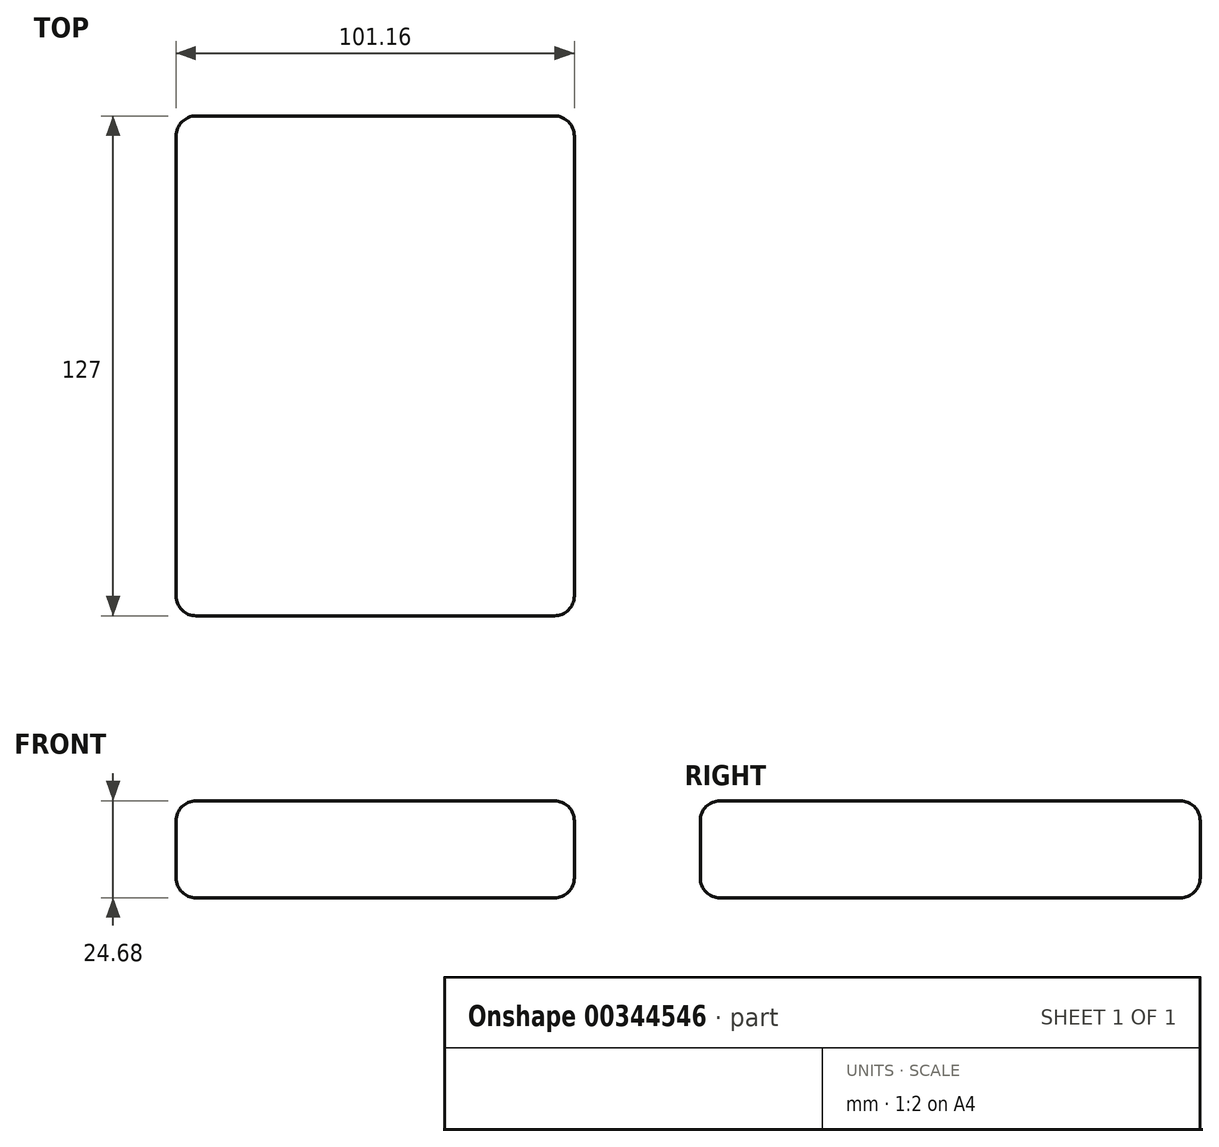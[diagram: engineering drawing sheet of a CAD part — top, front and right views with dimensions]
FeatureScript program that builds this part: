
annotation { "Feature Type Name" : "Feature", "Feature Type Description" : "" }
export const myFeature = defineFeature(function(context is Context, id is Id, definition is map)
    precondition{}
    {
        {
            var Q0;
            Q0=qCreatedBy(makeId("Front.planeOp"),FACE);
            var sketch = newSketch(context, id + "F0", { "sketchPlane" : qUnion([Q0])});
            skLineSegment(sketch, "E0.bottom", {"start": v(-50.58, 12.34) * mm, "end": v(50.58, 12.34) * mm});
            skLineSegment(sketch, "E0.top", {"start": v(-50.58, -12.34) * mm, "end": v(50.58, -12.34) * mm});
            skLineSegment(sketch, "E0.left", {"start": v(-50.58, 12.34) * mm, "end": v(-50.58, -12.34) * mm});
            skLineSegment(sketch, "E0.right", {"start": v(50.58, 12.34) * mm, "end": v(50.58, -12.34) * mm});
            skPoint(sketch, "E0.middle", {"position": v(0, 0) * mm});
            skSolve(sketch);
        }
        {
            var Q0;
            Q0 = qSketchRegion(id + "F0", true);
            var Q1;
            Q1 = qSketchRegion(id + "FBLzmxZTQiUzEOE_0", true);
            extrude(context, id + "F1", {"entities" : qUnion([Q0, Q1]), "endBound" : BoundingType.SYMMETRIC, "depth" : 127 * mm});
        }
        {
            var Q0;
            Q0=makeQuery(id+"F1.opExtrude","CAP_FACE",FACE,{"disambiguationData":[OSD([sQuery(id+"F0.wireOp",EDGE,"E0.bottom"),sQuery(id+"F0.wireOp",EDGE,"E0.top"),sQuery(id+"F0.wireOp",EDGE,"E0.left"),sQuery(id+"F0.wireOp",EDGE,"E0.right")])],"isStart":false});
            var Q1;
            Q1=makeQuery(id+"F1.opExtrude","SWEPT_FACE",FACE,{"disambiguationData":[OSD([sQuery(id+"F0.wireOp",EDGE,"E0.right")])]});
            var Q2;
            Q2=makeQuery(id+"F1.opExtrude","SWEPT_FACE",FACE,{"disambiguationData":[OSD([sQuery(id+"F0.wireOp",EDGE,"E0.left")])]});
            var Q3;
            Q3=makeQuery(id+"F1.opExtrude","CAP_FACE",FACE,{"disambiguationData":[OSD([sQuery(id+"F0.wireOp",EDGE,"E0.bottom"),sQuery(id+"F0.wireOp",EDGE,"E0.top"),sQuery(id+"F0.wireOp",EDGE,"E0.left"),sQuery(id+"F0.wireOp",EDGE,"E0.right")])],"isStart":true});
            var Q4;
            Q4=makeQuery(id+"F1.opExtrude","SWEPT_FACE",FACE,{"disambiguationData":[OSD([sQuery(id+"F0.wireOp",EDGE,"E0.bottom")])]});
            fillet(context, id + "F2", {"entities" : qUnion([Q0, Q1, Q2, Q3, Q4]), "radius" : 5.08 * mm, "tangentPropagation" : true, "allowEdgeOverflow" : false});
        }
    });
